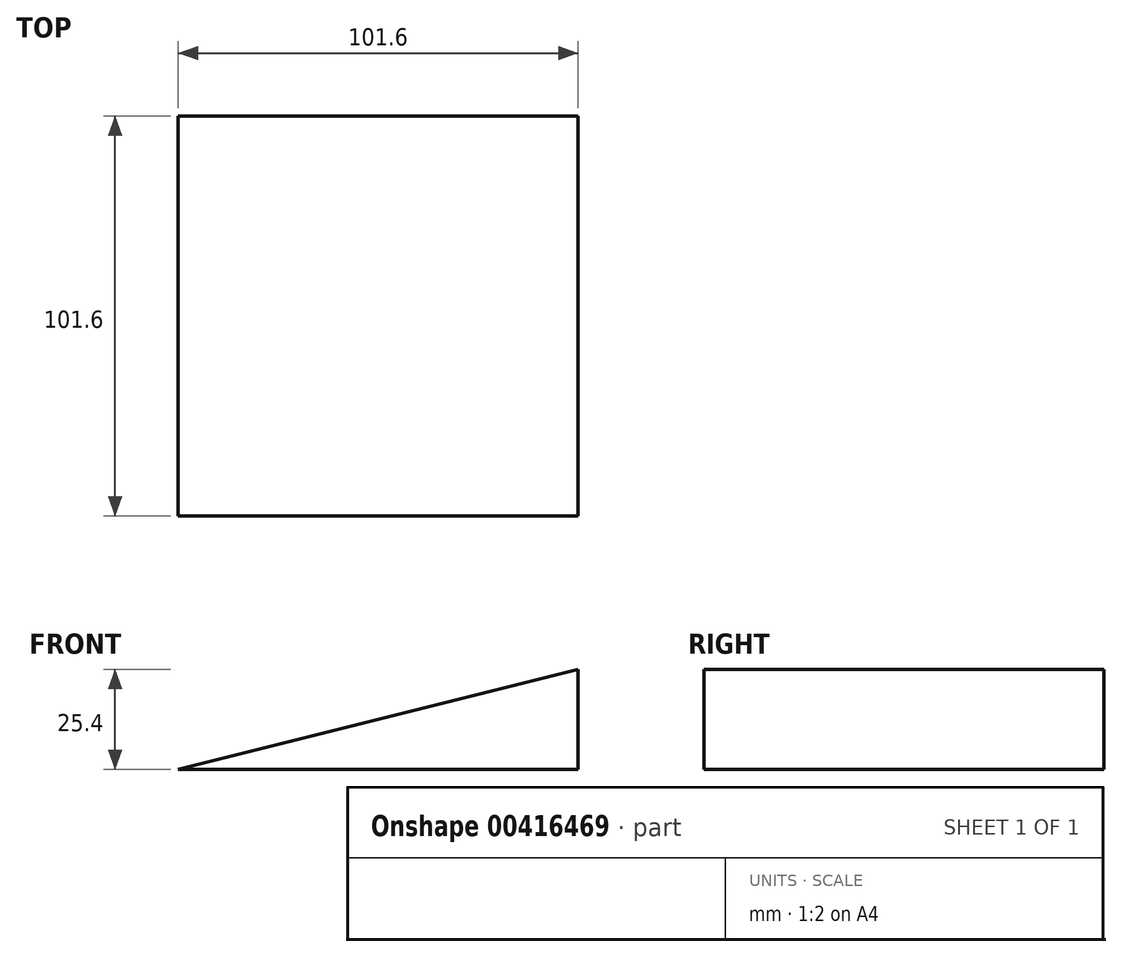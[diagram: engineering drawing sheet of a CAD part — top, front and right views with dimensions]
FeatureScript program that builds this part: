
annotation { "Feature Type Name" : "Feature", "Feature Type Description" : "" }
export const myFeature = defineFeature(function(context is Context, id is Id, definition is map)
    precondition{}
    {
        {
            var Q0;
            Q0=qCreatedBy(makeId("Front.planeOp"),FACE);
            var sketch = newSketch(context, id + "F0", { "sketchPlane" : qUnion([Q0])});
            skLineSegment(sketch, "E0", {"start": v(-91.15, -18.03) * mm, "end": v(10.45, -18.03) * mm});
            skLineSegment(sketch, "E1", {"start": v(10.45, -18.03) * mm, "end": v(10.45, 7.37) * mm});
            skLineSegment(sketch, "E2", {"start": v(10.45, 7.37) * mm, "end": v(-91.15, -18.03) * mm});
            skSolve(sketch);
        }
        {
            var Q0;
            Q0=makeQuery(id+"F0.imprint","IMPRINT",FACE,{"disambiguationData":[TD([[makeQuery(id+"F0.imprint","IMPRINT",EDGE,{"derivedFrom":sQuery(id+"F0.wireOp",EDGE,"E0")}),1.0]])]});
            extrude(context, id + "F1", {"entities" : qUnion([Q0]), "depth" : 101.6 * mm});
        }
    });
